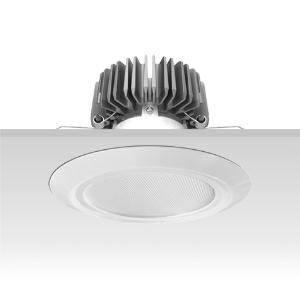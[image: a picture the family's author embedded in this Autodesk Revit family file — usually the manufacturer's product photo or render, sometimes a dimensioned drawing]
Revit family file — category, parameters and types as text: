
# Revit family: 3f_filippi_-_3f_reno_bianco_ampio_3f_filippi_-_30625_a01037_-_3f_reno_200_wh_2000-930_wide___vs_wh_4535
name_source: partatom
category: Lighting Fixtures
units: mm (PartAtom-declared; Revit-internal decimal feet)

## family parameters
Cut with Voids When Loaded = No
Host = Face
Light Source = No
Part Type = Normal
Room Calculation Point = No
Round Connector Dimension = Use Diameter
Shared = No

## types (1)
- 3F Filippi - 3F Reno Bianco Ampio (1 x LED, 1650 lm, 24 W, 3000 K)
    Apparent Load = 24 VA
    Approval mark = CE
    CIE Flux Codes = 75 94 99 100 100
    Color Rendering = 90
    Color Temperature = 3000 K
    Control Gear = Electronic ballast
    Default Elevation = 1800 mm
    Description = ILLUMINOTECHNICAL
Luminous efficiency 100% (DLOR 100%, ULOR 0%).
Initial luminous flux of the luminaire 1650 lm.
Direct symmetric wide distribution.
Installation Interdistance Transv.D = 1.16 x hu - Long.D = 1.14 x hu.
Average luminance <3000 cd/m² for radial angles >65°.
Tabular UGR (CIE 117 - 4H-8H; S=0.25H; 70/50/20): RUG 20.3 - 20.2.
Beam angle: 74° - 74°.
Luminous efficacy 69 lm/W.
Lifetime (L90/B10): 30000 h. (tq+25°C)
Lifetime (L85/B10): 50000 h. (tq+25°C)
Lifetime (L70/B10): 80000 h. (tq+25°C)
Sudden decreased luminous flux after 50000 hours: 0% (C0).
Photobiological safety in compliance with IEC/TR 62778: RG0 risk exempt, (IEC 62471).
In compliance with IEC/EN 62722-2-1 - IEC/EN 62717 standards.

SOURCE
Compact LED module 2000/930.
Energy efficiency class (UE 2019/2020 - UE 2019/2015): E.
CIE 13.3 Colour rendering index: CRI >90 (R9 >50%).
IES TM-30 Fidelity Index: Rf = 92 Rg = 101.
CCT nominal colour temperature 3000 K.
Colour initial tolerance (MacAdam): SDCM 3.
Zhaga Book 3 compliant.

MECHANICAL
Passive heat dissipator in die-casting aluminium, oversized, for optimum thermal management of the LED module.
Parabolic element with graduated/concentric rings in white polycarbonate.
Transparent external lens with glossy and satin differentiated surfaces, with a cooling and anti-insect system in methacrylate (PMMA).
Fastening spring clips in stainless steel.
Dimensions: diameter 226 mm, height 146 mm. Weight 1.165 kg.
IP44 protection degree for exposed part, IP20 for recessed part.
Mechanical strength to impacts IK06 (1 joule).
Glow-wire test resistance 650°C.

ELECTRICAL
Wiring on a separate unit.
Halogen Free electronic wiring 230V-50/60Hz, power factor 0.95, THD <25%, constant output current, SELV, class II, 1 driver.
Power of the luminaire 24 W.
ENEC - CE.
SAFE FLICKER: PstLM=<1 and SVM=<0.4 (IEC TR 61547-1 and IEC TR 63158), to ensure a more comfortable and safe light.
Luminaire compliant with EN 60598-2-22 for power supply from a centralised emergency system CPSS (Central Power Supply System), not incorporated in the luminaire - high risk areas excluded. The default power and flux are 100% in AC and 100% in DC.
Ambient temperature from 0°C to +25°C.
Temperature class T6 max 85°C.
Relative humidity UR: <85%.

INSTALLATION
Pull-up recessed fitting.
False ceiling carving: 200 mm.
All accessories dedicated to this product are available on the Catalog and on our website www.3F-Filippi.com.

ACCESSORIES
A01037 - Anti-glare microprismatic VS moulded glass, tempered, not flammable, locked and in line with the trim, in white polycarbonate.

APPLICATIONS
Environments: architectural, commercial, exhibition areas, transit areas, corridors, shops, display windows, service areas.
In false ceilings with narrow voids.

WARNING
Luminaire designed for disposal/recycling at end-of-life.
Replaceable (LED only) light source by a professional. Replaceable control gear by a professional.
    Height = 0 mm  [stored 0 ft]
    Lamp = 1 x LED
    Lamp Light Flux = 1650 lm
    Lamp Power = 24 W
    Lamp count = 1
    Length = 226 mm
    Lifetime = 50000 h
    Luminous efficacy = 69 lm/W
    Manufacturer = 3F Filippi
    ModVariant = No
    Model = 3F Filippi - 30625+A01037 - 3F Reno 200 WH 2000-930 WIDE + VS WH
    Mounting Place = Ceiling
    Mounting Type = Recessed
    Number of Poles = 1
    OnlyDefault = Yes
    Power Factor = 1
    Product Name = 3F Filippi - 3F Reno Bianco Ampio
    Product group = recessed luminaire
    ProductGroupID = 4
    Protection Class = Protection class II
    Protection Degree = IP 20
    RLX_Detail_Level = 1
    RLX_Emergency_Light_Flux = 0 lm
    RLX_Emergency_Type = 0
    RLX_Emergency_Type_DB = No
    RlxData = <blob elided: 94829 chars, md5=095549b3>
    Socket = socket
    Standby Power = 0 W
    System Light Flux = 1650 lm
    System Power = 24 W
    Type Comments = Product without accessories
    Type Image = 3ffilippi_3f_reno_200_wh_vs_smp.jpg
    URL = http://relux.com
    VarID = ---
    Voltage = 0 V
    Weight = 0.00 kg
    Width = 0 mm  [stored 0 ft]

note: [stored X ft] marks values corroborated as IEEE doubles in the binary element streams (Revit-internal decimal feet)

## geometry (parser evidence)
native form markers: Blend x4, Sweep x10
no freeform markers — native parametric forms only
